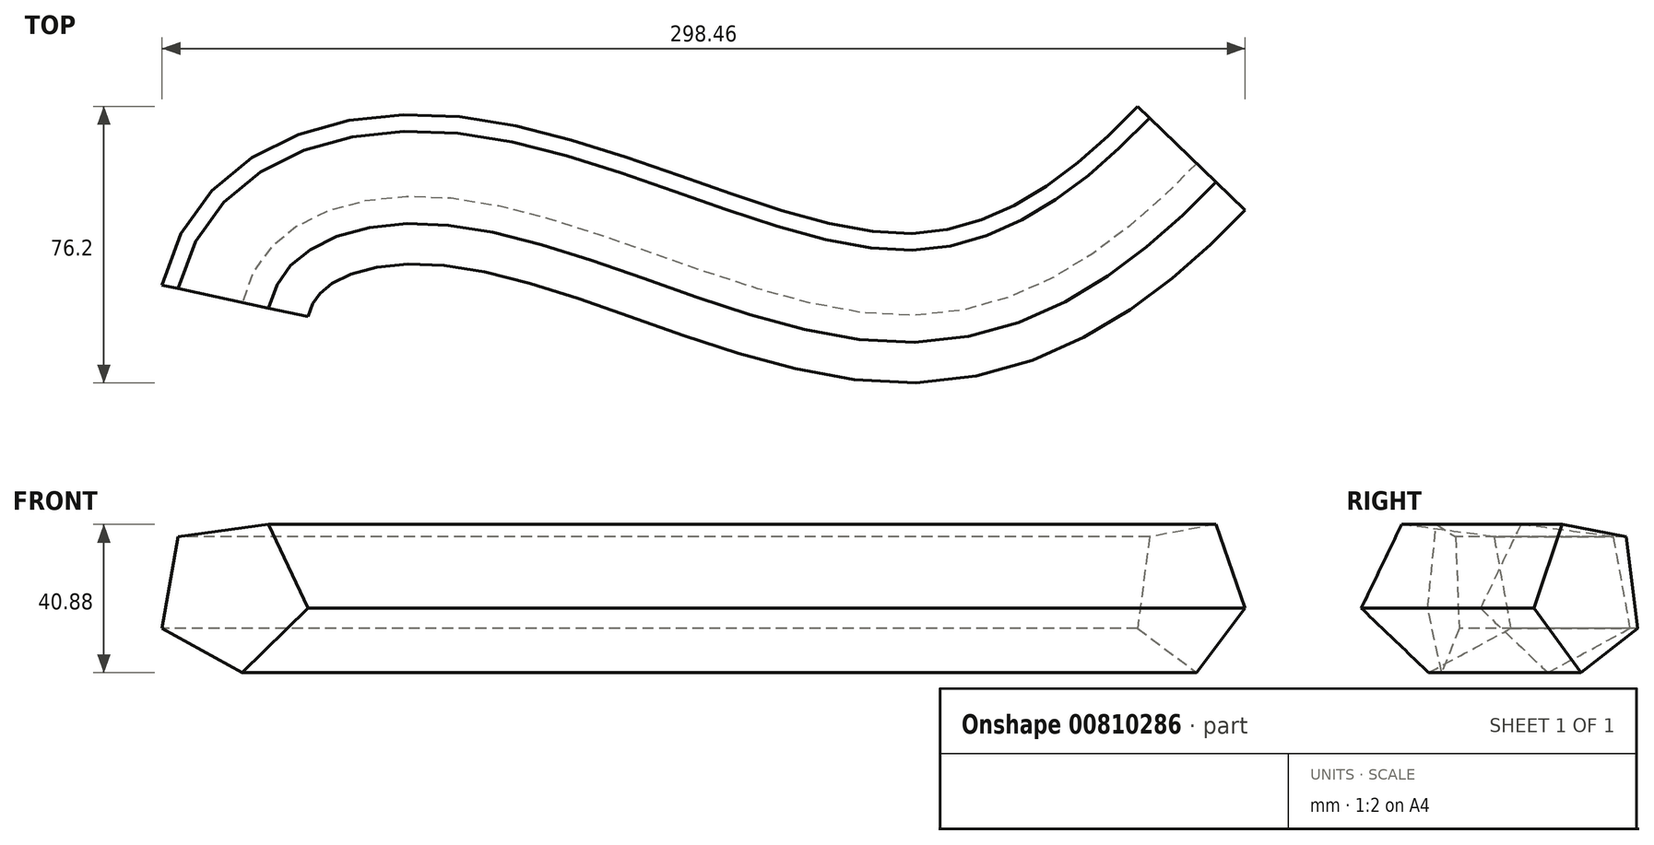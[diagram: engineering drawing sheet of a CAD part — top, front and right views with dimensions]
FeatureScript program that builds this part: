
annotation { "Feature Type Name" : "Feature", "Feature Type Description" : "" }
export const myFeature = defineFeature(function(context is Context, id is Id, definition is map)
    precondition{}
    {
        {
            var Q0;
            Q0=qCreatedBy(makeId("Top.planeOp"),FACE);
            var sketch = newSketch(context, id + "F0", { "sketchPlane" : qUnion([Q0])});
            skFitSpline(sketch, "E0", {"points": [v(-161, -36.47) * mm, v(-95.7, 0) * mm, v(30.96, -32.51) * mm, v(104.46, 6.5) * mm], "startDerivative": vector(58.44, 271.62) * mm, "endDerivative": vector(193.22, 200.74) * mm});
            skSolve(sketch);
        }
        {
            var Q0;
            Q0=sQuery(id+"F0.wireOp",VERTEX,"E0.end");
            var Q1;
            Q1=sQuery(id+"F0.wireOp",EDGE,"E0");
            cPlane(context, id + "F1", {"entities" : qUnion([Q0, Q1]), "cplaneType" : CPlaneType.CURVE_POINT, "offset" : 25 * mm, "width" : 150 * mm, "height" : 150 * mm});
        }
        {
            var Q0;
            Q0=qCreatedBy(id+"F1.planeOp",FACE);
            var sketch = newSketch(context, id + "F2", { "sketchPlane" : qUnion([Q0])});
            skCircle(sketch, "E1.cCircle", {"center": v(-77.44, -22.39) * mm, "radius": 17.67 * mm, "construction": true});
            skLineSegment(sketch, "E1.0", {"start": v(-87.79, -3.15) * mm, "end": v(-62.35, -6.6) * mm});
            skLineSegment(sketch, "E1.1", {"start": v(-62.35, -6.6) * mm, "end": v(-57.76, -31.87) * mm});
            skLineSegment(sketch, "E1.2", {"start": v(-57.76, -31.87) * mm, "end": v(-80.37, -44.03) * mm});
            skLineSegment(sketch, "E1.3", {"start": v(-80.37, -44.03) * mm, "end": v(-98.93, -26.29) * mm});
            skLineSegment(sketch, "E1.4", {"start": v(-98.93, -26.29) * mm, "end": v(-87.79, -3.15) * mm});
            skPoint(sketch, "E1.0.midPoint", {"position": v(-75.07, -4.88) * mm});
            skSolve(sketch);
        }
        {
            var Q0;
            Q0=makeQuery(id+"F2.imprint","IMPRINT",FACE,{"disambiguationData":[TD([[makeQuery(id+"F2.imprint","IMPRINT",EDGE,{"derivedFrom":sQuery(id+"F2.wireOp",EDGE,"E1.0")}),-1.0]])]});
            var Q1;
            Q1=sQuery(id+"F0.wireOp",EDGE,"E0");
            sweep(context, id + "F3", {"profiles" : qUnion([Q0]), "path" : qUnion([Q1])});
        }
    });
